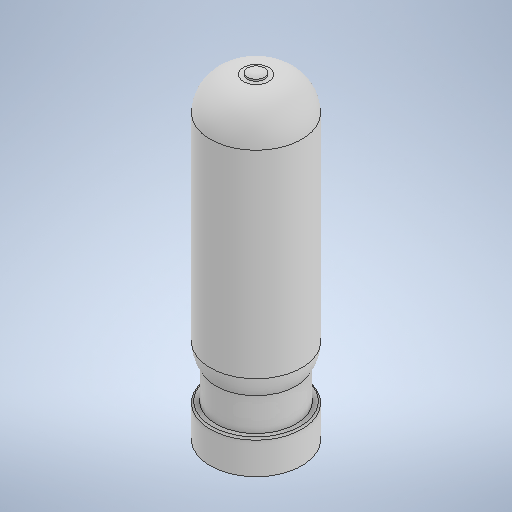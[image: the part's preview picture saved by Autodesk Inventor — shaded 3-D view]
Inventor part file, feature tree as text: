
AUTODESK INVENTOR PART (.ipt)
format: ipt  version: 2025 (Build 290162010, 162A)  size: 279,040 bytes
history: native  units: mm
features: revolve x1, chamfer x1, sketch x1
ambient origin geometry x8: Origin, YZ Plane, XZ Plane, XY Plane, X Axis, Y Axis, Z Axis, Center Point
bodies: Solid1 (feature_tree)
feature tree (3):
  revolve  "Revolution1"  [1 undecoded]
  chamfer  "Chamfer1"  Distance=200.0mm
  sketch  "Sketch2"  dims[d3=550.0mm d7=200.0mm d8=200.0mm d9=35.0mm d10=200.0mm d11=360.0deg d12=50.0mm d13=10.0mm d14=1910.0mm d15=1600.0mm d16=10.0mm d17=2.0mm d18=45.0deg]
note: 1 required parameter value undecoded (feature->parameter linkage not recoverable at this tier; creation-order binding heuristic only, values carry confidence <= 0.55)
